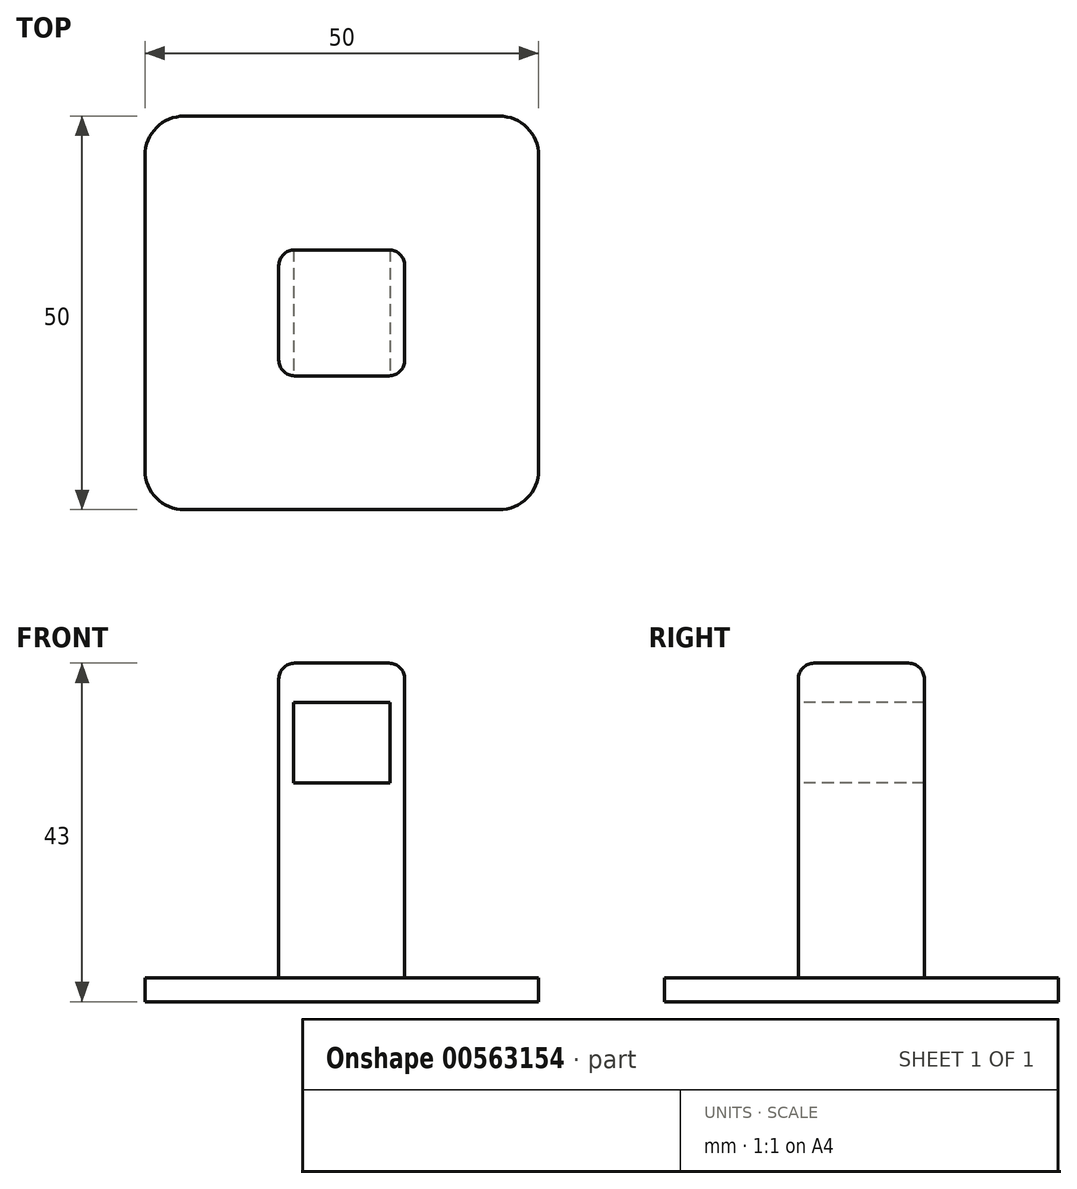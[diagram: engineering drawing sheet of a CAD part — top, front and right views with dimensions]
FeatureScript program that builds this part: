
annotation { "Feature Type Name" : "Feature", "Feature Type Description" : "" }
export const myFeature = defineFeature(function(context is Context, id is Id, definition is map)
    precondition{}
    {
        {
            var Q0;
            Q0=qCreatedBy(makeId("Top.planeOp"),FACE);
            var sketch = newSketch(context, id + "F0", { "sketchPlane" : qUnion([Q0])});
            skLineSegment(sketch, "E0.bottom", {"start": v(0, 0) * mm, "end": v(50, 0) * mm});
            skLineSegment(sketch, "E0.top", {"start": v(0, 50) * mm, "end": v(50, 50) * mm});
            skLineSegment(sketch, "E0.left", {"start": v(0, 0) * mm, "end": v(0, 50) * mm});
            skLineSegment(sketch, "E0.right", {"start": v(50, 0) * mm, "end": v(50, 50) * mm});
            skSolve(sketch);
        }
        {
            var Q0;
            Q0=makeQuery(id+"F0.imprint","IMPRINT",FACE,{"disambiguationData":[TD([[makeQuery(id+"F0.imprint","IMPRINT",EDGE,{"derivedFrom":sQuery(id+"F0.wireOp",EDGE,"E0.bottom")}),1.0]])]});
            extrude(context, id + "F1", {"entities" : qUnion([Q0]), "depth" : 3 * mm, "offsetDistance" : 25 * mm});
        }
        {
            var Q0;
            Q0=makeQuery(id+"F1.opExtrude","CAP_FACE",FACE,{"disambiguationData":[OSD([sQuery(id+"F0.wireOp",EDGE,"E0.bottom"),sQuery(id+"F0.wireOp",EDGE,"E0.top"),sQuery(id+"F0.wireOp",EDGE,"E0.left"),sQuery(id+"F0.wireOp",EDGE,"E0.right")])],"isStart":false});
            var sketch = newSketch(context, id + "F2", { "sketchPlane" : qUnion([Q0])});
            skLineSegment(sketch, "E1.bottom", {"start": v(17, 33) * mm, "end": v(33, 33) * mm});
            skLineSegment(sketch, "E1.top", {"start": v(17, 17) * mm, "end": v(33, 17) * mm});
            skLineSegment(sketch, "E1.left", {"start": v(17, 33) * mm, "end": v(17, 17) * mm});
            skLineSegment(sketch, "E1.right", {"start": v(33, 33) * mm, "end": v(33, 17) * mm});
            skSolve(sketch);
        }
        {
            var Q0;
            Q0=makeQuery(id+"F2.imprint","IMPRINT",FACE,{"disambiguationData":[TD([[makeQuery(id+"F2.imprint","IMPRINT",EDGE,{"derivedFrom":sQuery(id+"F2.wireOp",EDGE,"E1.bottom")}),-1.0]])]});
            extrude(context, id + "F3", {"entities" : qUnion([Q0]), "operationType" : NewBodyOperationType.ADD, "depth" : 40 * mm, "offsetDistance" : 25 * mm});
        }
        {
            var Q0;
            Q0=makeQuery(id+"F3.opExtrude","SWEPT_FACE",FACE,{"disambiguationData":[OSD([sQuery(id+"F2.wireOp",EDGE,"E1.top")])]});
            var sketch = newSketch(context, id + "F4", { "sketchPlane" : qUnion([Q0])});
            skLineSegment(sketch, "E2.bottom", {"start": v(18.9, 38) * mm, "end": v(31.1, 38) * mm});
            skLineSegment(sketch, "E2.top", {"start": v(18.9, 27.8) * mm, "end": v(31.1, 27.8) * mm});
            skLineSegment(sketch, "E2.left", {"start": v(18.9, 38) * mm, "end": v(18.9, 27.8) * mm});
            skLineSegment(sketch, "E2.right", {"start": v(31.1, 38) * mm, "end": v(31.1, 27.8) * mm});
            skSolve(sketch);
        }
        {
            var Q0;
            Q0=makeQuery(id+"F4.imprint","IMPRINT",FACE,{"disambiguationData":[TD([[makeQuery(id+"F4.imprint","IMPRINT",EDGE,{"derivedFrom":sQuery(id+"F4.wireOp",EDGE,"E2.bottom")}),-1.0]])]});
            extrude(context, id + "F5", {"entities" : qUnion([Q0]), "operationType" : NewBodyOperationType.REMOVE, "oppositeDirection" : true, "depth" : 16 * mm, "offsetDistance" : 25 * mm});
        }
        {
            var Q0;
            Q0=makeQuery(id+"F3.opExtrude","CAP_EDGE",EDGE,{"disambiguationData":[OSD([sQuery(id+"F2.wireOp",EDGE,"E1.top")])],"isStart":false});
            var Q1;
            Q1=makeQuery(id+"F3.opExtrude","CAP_EDGE",EDGE,{"disambiguationData":[OSD([sQuery(id+"F2.wireOp",EDGE,"E1.right")])],"isStart":false});
            var Q2;
            Q2=makeQuery(id+"F3.opExtrude","CAP_EDGE",EDGE,{"disambiguationData":[OSD([sQuery(id+"F2.wireOp",EDGE,"E1.bottom")])],"isStart":false});
            var Q3;
            Q3=makeQuery(id+"F3.opExtrude","CAP_EDGE",EDGE,{"disambiguationData":[OSD([sQuery(id+"F2.wireOp",EDGE,"E1.left")])],"isStart":false});
            var Q4;
            Q4=makeQuery(id+"F3.opExtrude","SWEPT_EDGE",EDGE,{"disambiguationData":[OSD([sQuery(id+"F2.wireOp",EDGE,"E1.top"),sQuery(id+"F2.wireOp",EDGE,"E1.right")])]});
            var Q5;
            Q5=makeQuery(id+"F3.opExtrude","SWEPT_EDGE",EDGE,{"disambiguationData":[OSD([sQuery(id+"F2.wireOp",EDGE,"E1.bottom"),sQuery(id+"F2.wireOp",EDGE,"E1.right")])]});
            var Q6;
            Q6=makeQuery(id+"F3.opExtrude","SWEPT_EDGE",EDGE,{"disambiguationData":[OSD([sQuery(id+"F2.wireOp",EDGE,"E1.top"),sQuery(id+"F2.wireOp",EDGE,"E1.left")])]});
            var Q7;
            Q7=makeQuery(id+"F3.opExtrude","CAP_EDGE",EDGE,{"disambiguationData":[OSD([sQuery(id+"F2.wireOp",EDGE,"E1.top")])],"isStart":true});
            var Q8;
            Q8=makeQuery(id+"F3.opExtrude","CAP_EDGE",EDGE,{"disambiguationData":[OSD([sQuery(id+"F2.wireOp",EDGE,"E1.right")])],"isStart":true});
            var Q9;
            Q9=makeQuery(id+"F3.opExtrude","CAP_EDGE",EDGE,{"disambiguationData":[OSD([sQuery(id+"F2.wireOp",EDGE,"E1.left")])],"isStart":true});
            var Q10;
            Q10=makeQuery(id+"F3.opExtrude","SWEPT_EDGE",EDGE,{"disambiguationData":[OSD([sQuery(id+"F2.wireOp",EDGE,"E1.bottom"),sQuery(id+"F2.wireOp",EDGE,"E1.left")])]});
            var Q11;
            Q11=makeQuery(id+"F3.opExtrude","CAP_EDGE",EDGE,{"disambiguationData":[OSD([sQuery(id+"F2.wireOp",EDGE,"E1.bottom")])],"isStart":true});
            fillet(context, id + "F6", {"entities" : qUnion([Q0, Q1, Q2, Q3, Q4, Q5, Q6, Q7, Q8, Q9, Q10, Q11]), "radius" : 2 * mm, "tangentPropagation" : true, "allowEdgeOverflow" : false});
        }
        {
            var Q0;
            Q0=makeQuery(id+"F1.opExtrude","SWEPT_EDGE",EDGE,{"disambiguationData":[OSD([sQuery(id+"F0.wireOp",EDGE,"E0.bottom"),sQuery(id+"F0.wireOp",EDGE,"E0.left")])]});
            var Q1;
            Q1=makeQuery(id+"F1.opExtrude","SWEPT_EDGE",EDGE,{"disambiguationData":[OSD([sQuery(id+"F0.wireOp",EDGE,"E0.bottom"),sQuery(id+"F0.wireOp",EDGE,"E0.right")])]});
            var Q2;
            Q2=makeQuery(id+"F1.opExtrude","SWEPT_EDGE",EDGE,{"disambiguationData":[OSD([sQuery(id+"F0.wireOp",EDGE,"E0.top"),sQuery(id+"F0.wireOp",EDGE,"E0.left")])]});
            var Q3;
            Q3=makeQuery(id+"F1.opExtrude","SWEPT_EDGE",EDGE,{"disambiguationData":[OSD([sQuery(id+"F0.wireOp",EDGE,"E0.top"),sQuery(id+"F0.wireOp",EDGE,"E0.right")])]});
            fillet(context, id + "F7", {"entities" : qUnion([Q0, Q1, Q2, Q3]), "radius" : 5 * mm, "tangentPropagation" : true, "allowEdgeOverflow" : false});
        }
    });
